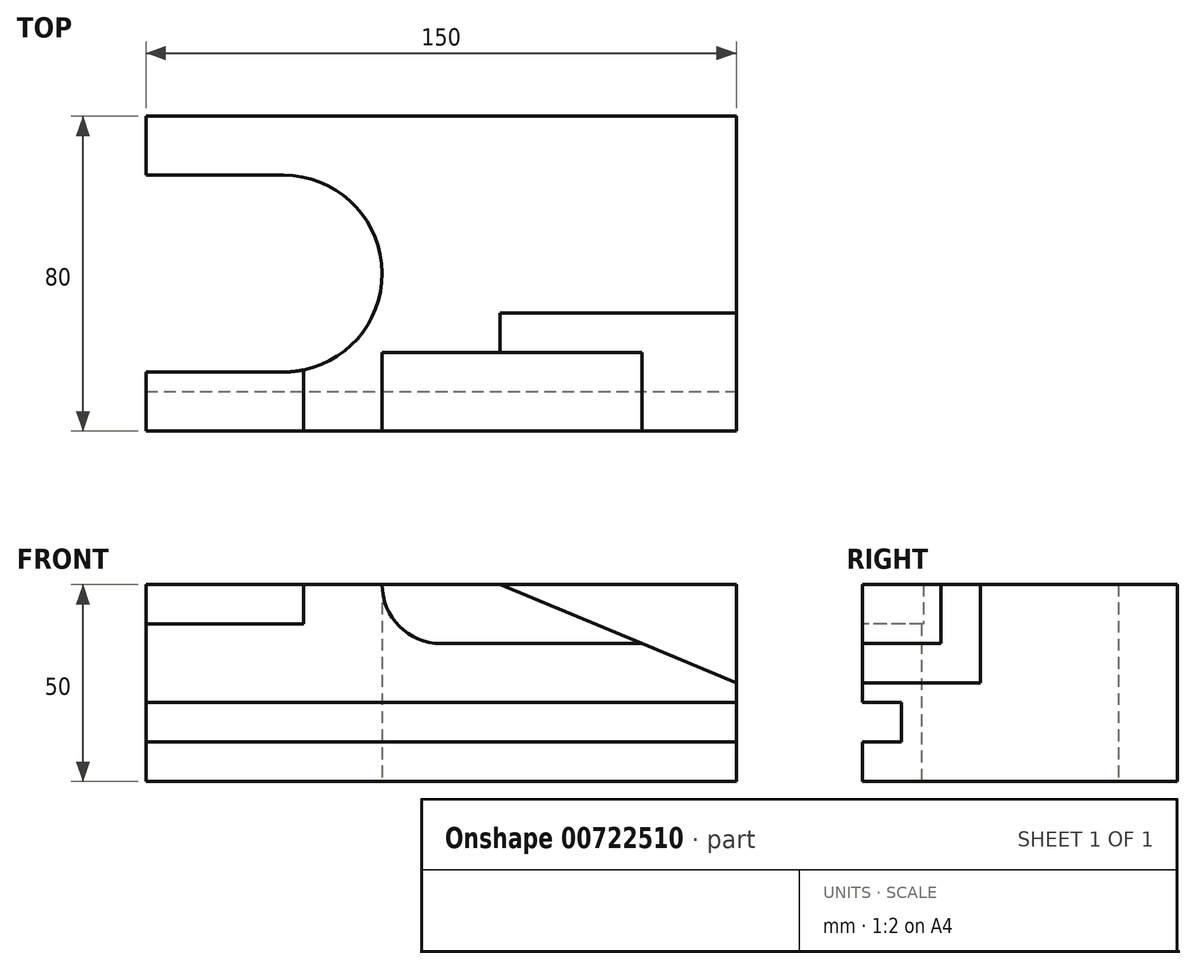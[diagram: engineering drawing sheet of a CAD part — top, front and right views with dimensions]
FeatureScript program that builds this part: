
annotation { "Feature Type Name" : "Feature", "Feature Type Description" : "" }
export const myFeature = defineFeature(function(context is Context, id is Id, definition is map)
    precondition{}
    {
        {
            var Q0;
            Q0=qCreatedBy(makeId("Top.planeOp"),FACE);
            var sketch = newSketch(context, id + "F0", { "sketchPlane" : qUnion([Q0])});
            skLineSegment(sketch, "E0.bottom", {"start": v(-35, -40) * mm, "end": v(115, -40) * mm});
            skLineSegment(sketch, "E0.top", {"start": v(-35, 40) * mm, "end": v(115, 40) * mm});
            skLineSegment(sketch, "E0.left", {"start": v(-35, -40) * mm, "end": v(-35, -25) * mm});
            skLineSegment(sketch, "E0.right", {"start": v(115, -40) * mm, "end": v(115, 40) * mm});
            skLineSegment(sketch, "E1", {"start": v(-35, 0) * mm, "end": v(0, 0) * mm, "construction": true});
            skArc(sketch, "E2.0.startCap", {"start": v(0, 25) * mm, "mid": v(25, 0) * mm, "end": v(0, -25) * mm});
            skLineSegment(sketch, "E2.0.left", {"start": v(-35, -25) * mm, "end": v(0, -25) * mm});
            skLineSegment(sketch, "E2.0.right", {"start": v(-35, 25) * mm, "end": v(0, 25) * mm});
            skLineSegment(sketch, "E3.trimOffspring", {"start": v(-35, 25) * mm, "end": v(-35, 40) * mm});
            skSolve(sketch);
        }
        {
            var Q0;
            Q0=qSketchRegion(id+"F0",true);
            extrude(context, id + "F1", {"entities" : qUnion([Q0]), "depth" : 50 * mm, "offsetDistance" : 25 * mm});
        }
        {
            var Q0;
            Q0=makeQuery(id+"F1.opExtrude","SWEPT_FACE",FACE,{"disambiguationData":[OSD([sQuery(id+"F0.wireOp",EDGE,"E0.bottom")])]});
            var sketch = newSketch(context, id + "F2", { "sketchPlane" : qUnion([Q0])});
            skLineSegment(sketch, "E4.bottom", {"start": v(-35, 50) * mm, "end": v(5, 50) * mm});
            skLineSegment(sketch, "E4.top", {"start": v(-35, 40) * mm, "end": v(5, 40) * mm});
            skLineSegment(sketch, "E4.left", {"start": v(-35, 50) * mm, "end": v(-35, 40) * mm});
            skLineSegment(sketch, "E4.right", {"start": v(5, 50) * mm, "end": v(5, 40) * mm});
            skLineSegment(sketch, "E5", {"start": v(-35, 10) * mm, "end": v(115, 10) * mm});
            skLineSegment(sketch, "E6", {"start": v(-35, 20) * mm, "end": v(115, 20) * mm});
            skLineSegment(sketch, "E7", {"start": v(115, 25) * mm, "end": v(55, 50) * mm});
            skArc(sketch, "E8", {"start": v(25, 50) * mm, "mid": v(29.4, 39.4) * mm, "end": v(40, 35) * mm});
            skLineSegment(sketch, "E9", {"start": v(40, 35) * mm, "end": v(91, 35) * mm});
            skLineSegment(sketch, "E10.0", {"start": v(115, 50) * mm, "end": v(115, 0) * mm});
            skSolve(sketch);
        }
        {
            var Q0;
            Q0=makeQuery(id+"F2.imprint","IMPRINT",FACE,{"disambiguationData":[TD([[makeQuery(id+"F2.imprint","IMPRINT",EDGE,{"derivedFrom":sQuery(id+"F2.wireOp",EDGE,"E4.bottom")}),-1.0]])]});
            var Q1;
            {var subQ0=sQuery(id+"F2.wireOp",EDGE,"E10.0");var subQ1=sQuery(id+"F2.wireOp",EDGE,"E7");var subQ2=makeQuery(id+"F2.imprint","INTERSECT",VERTEX,{"derivedFrom":[subQ1,subQ0]});Q1=makeQuery(id+"F2.imprint","IMPRINT",FACE,{"disambiguationData":[TD([[makeQuery(id+"F2.imprint","IMPRINT",EDGE,{"disambiguationData":[TD([[subQ2,-1.0]])],"derivedFrom":subQ1}),-1.0]])]});}
            extrude(context, id + "F3", {"entities" : qUnion([Q0, Q1]), "operationType" : NewBodyOperationType.REMOVE, "oppositeDirection" : true, "depth" : 30 * mm, "offsetDistance" : 25 * mm});
        }
        {
            var Q0;
            {var subQ0=sQuery(id+"F2.wireOp",EDGE,"E5");Q0=makeQuery(id+"F2.imprint","IMPRINT",FACE,{"disambiguationData":[TD([[makeQuery(id+"F2.imprint","IMPRINT",EDGE,{"derivedFrom":subQ0}),1.0]])]});}
            extrude(context, id + "F4", {"entities" : qUnion([Q0]), "operationType" : NewBodyOperationType.REMOVE, "oppositeDirection" : true, "depth" : 10 * mm, "offsetDistance" : 25 * mm});
        }
        {
            var Q0;
            {var subQ4=sQuery(id+"F2.wireOp",EDGE,"E8");Q0=makeQuery(id+"F2.imprint","IMPRINT",FACE,{"disambiguationData":[TD([[makeQuery(id+"F2.imprint","IMPRINT",EDGE,{"derivedFrom":subQ4}),1.0]])]});}
            extrude(context, id + "F5", {"entities" : qUnion([Q0]), "operationType" : NewBodyOperationType.REMOVE, "oppositeDirection" : true, "depth" : 20 * mm, "offsetDistance" : 25 * mm});
        }
    });
